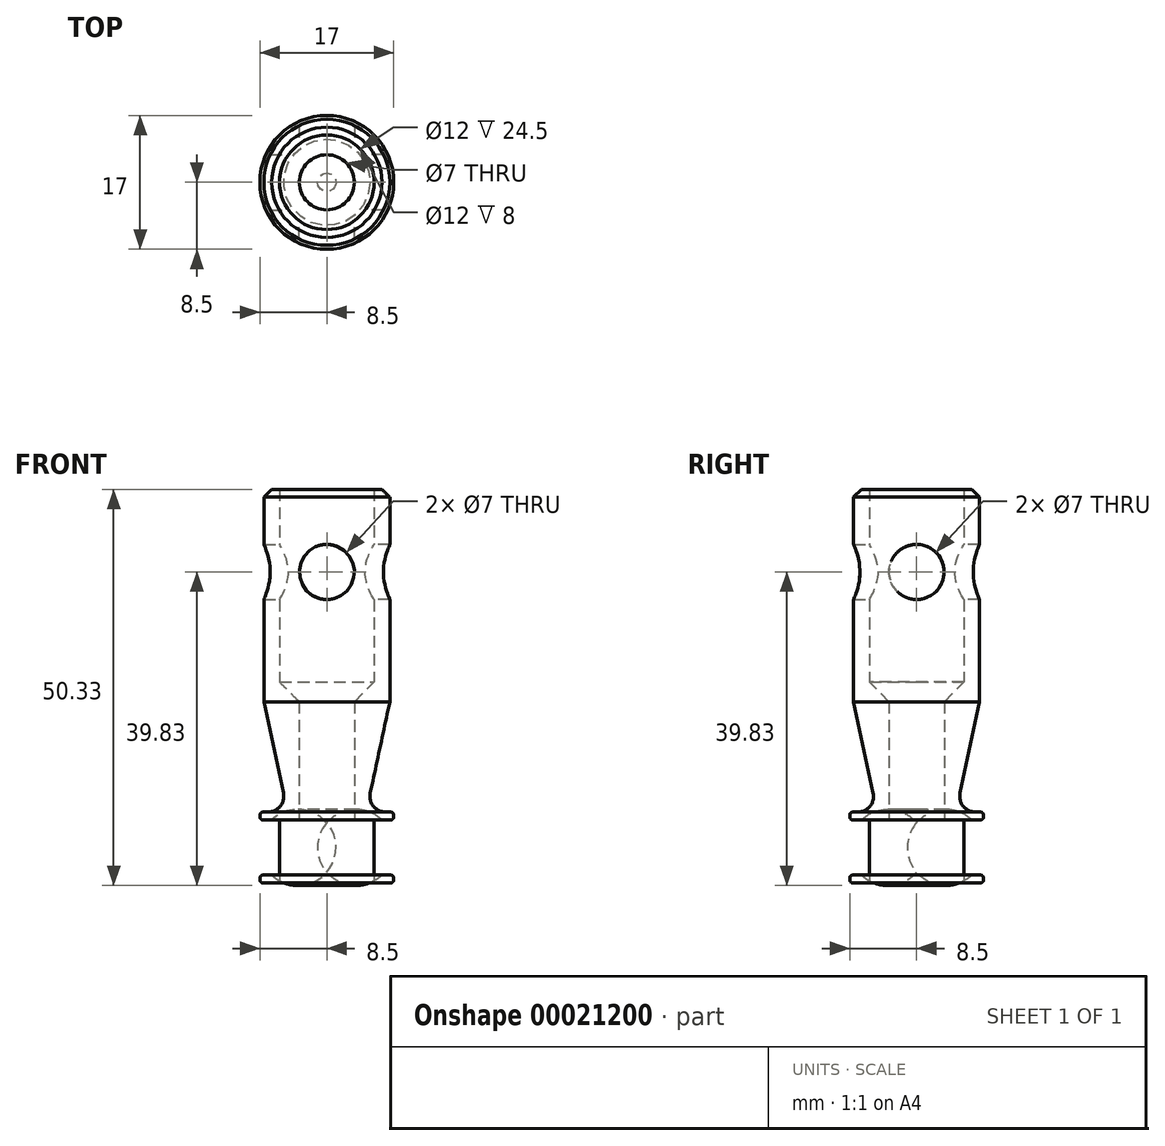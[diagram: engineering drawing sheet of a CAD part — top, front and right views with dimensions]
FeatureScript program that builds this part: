
annotation { "Feature Type Name" : "Feature", "Feature Type Description" : "" }
export const myFeature = defineFeature(function(context is Context, id is Id, definition is map)
    precondition{}
    {
        {
            var Q0;
            Q0=qCreatedBy(makeId("Front.planeOp"),FACE);
            var sketch = newSketch(context, id + "F0", { "sketchPlane" : qUnion([Q0])});
            skLineSegment(sketch, "E0", {"start": v(6, 0) * mm, "end": v(8.5, 0) * mm});
            skLineSegment(sketch, "E1", {"start": v(8.5, 0) * mm, "end": v(8.5, 1) * mm});
            skLineSegment(sketch, "E2", {"start": v(8.5, 1) * mm, "end": v(7, 1) * mm});
            skArc(sketch, "E3", {"start": v(7, 1) * mm, "mid": v(8.5, 4.5) * mm, "end": v(7, 8) * mm});
            skLineSegment(sketch, "E4", {"start": v(7, 8) * mm, "end": v(8.5, 8) * mm});
            skLineSegment(sketch, "E5", {"start": v(8.5, 8) * mm, "end": v(8.5, 9) * mm});
            skLineSegment(sketch, "E6", {"start": v(8.5, 9) * mm, "end": v(5, 9) * mm});
            skLineSegment(sketch, "E7", {"start": v(5, 9) * mm, "end": v(8, 23) * mm});
            skLineSegment(sketch, "E8", {"start": v(8, 23) * mm, "end": v(8, 50) * mm});
            skLineSegment(sketch, "E9", {"start": v(8, 50) * mm, "end": v(6, 50) * mm});
            skLineSegment(sketch, "E10", {"start": v(6, 50) * mm, "end": v(6, 25.5) * mm});
            skLineSegment(sketch, "E11", {"start": v(6, 25.5) * mm, "end": v(3.5, 23) * mm});
            skLineSegment(sketch, "E12", {"start": v(3.5, 23) * mm, "end": v(3.5, 8) * mm});
            skLineSegment(sketch, "E13", {"start": v(3.5, 8) * mm, "end": v(6, 8) * mm});
            skLineSegment(sketch, "E14", {"start": v(6, 8) * mm, "end": v(6, 0) * mm});
            skLineSegment(sketch, "E15", {"start": v(0, 0) * mm, "end": v(0, 60.76) * mm, "construction": true});
            skPoint(sketch, "E16", {"position": v(8.5, 4.5) * mm});
            skSolve(sketch);
        }
        {
            var Q0;
            Q0=qSketchRegion(id+"F0",true);
            var Q1;
            Q1=sQuery(id+"F0.wireOp",EDGE,"E15");
            revolve(context, id + "F1", {"entities" : qUnion([Q0]), "axis" : qUnion([Q1]), "revolveType" : RevolveType.FULL});
        }
        {
            var Q0;
            Q0=makeQuery(id+"F1.opRevolve","SWEPT_EDGE",EDGE,{"disambiguationData":[OSD([sQuery(id+"F0.wireOp",EDGE,"E6"),sQuery(id+"F0.wireOp",EDGE,"E7")])]});
            fillet(context, id + "F2", {"entities" : qUnion([Q0]), "radius" : 2 * mm, "tangentPropagation" : true, "allowEdgeOverflow" : false});
        }
        {
            var Q0;
            Q0=makeQuery(id+"F1.opRevolve","SWEPT_EDGE",EDGE,{"disambiguationData":[OSD([sQuery(id+"F0.wireOp",EDGE,"E0"),sQuery(id+"F0.wireOp",EDGE,"E1")])]});
            var Q1;
            Q1=makeQuery(id+"F1.opRevolve","SWEPT_EDGE",EDGE,{"disambiguationData":[OSD([sQuery(id+"F0.wireOp",EDGE,"E1"),sQuery(id+"F0.wireOp",EDGE,"E2")])]});
            var Q2;
            Q2=makeQuery(id+"F1.opRevolve","SWEPT_EDGE",EDGE,{"disambiguationData":[OSD([sQuery(id+"F0.wireOp",EDGE,"E4"),sQuery(id+"F0.wireOp",EDGE,"E5")])]});
            var Q3;
            Q3=makeQuery(id+"F1.opRevolve","SWEPT_EDGE",EDGE,{"disambiguationData":[OSD([sQuery(id+"F0.wireOp",EDGE,"E5"),sQuery(id+"F0.wireOp",EDGE,"E6")])]});
            fillet(context, id + "F3", {"entities" : qUnion([Q0, Q1, Q2, Q3]), "radius" : 0.4 * mm, "tangentPropagation" : true, "allowEdgeOverflow" : false});
        }
        {
            var Q0;
            Q0=qCreatedBy(makeId("Front.planeOp"),FACE);
            var sketch = newSketch(context, id + "F4", { "sketchPlane" : qUnion([Q0])});
            skCircle(sketch, "E17", {"center": v(0, 39.5) * mm, "radius": 3.5 * mm});
            skSolve(sketch);
        }
        {
            var Q0;
            Q0=qSketchRegion(id+"F4",true);
            extrude(context, id + "F5", {"entities" : qUnion([Q0]), "operationType" : NewBodyOperationType.REMOVE, "endBound" : BoundingType.THROUGH_ALL, "oppositeDirection" : true, "depth" : 25 * mm});
        }
        {
            var Q0;
            Q0=makeQuery(id+"F5.boolean.opBoolean","COPY",FACE,{"derivedFrom":makeQuery(id+"F5.opExtrude","SWEPT_FACE",FACE,{"disambiguationData":[OSD([sQuery(id+"F4.wireOp",EDGE,"E17")])]})});
            var Q1;
            Q1=makeQuery(id+"F1.opRevolve","SWEPT_FACE",FACE,{"disambiguationData":[OSD([sQuery(id+"F0.wireOp",EDGE,"E10")])]});
            circularPattern(context, id + "F6", {"faces" : qUnion([Q0]), "axis" : qUnion([Q1]), "angle" : 360 * degree, "instanceCount" : round(4), "equalSpace" : true, "patternType" : PatternType.FACE});
        }
        {
            var Q0;
            Q0=makeQuery(id+"F1.opRevolve","SWEPT_EDGE",EDGE,{"disambiguationData":[OSD([sQuery(id+"F0.wireOp",EDGE,"E8"),sQuery(id+"F0.wireOp",EDGE,"E9")])]});
            chamfer(context, id + "F7", {"entities" : qUnion([Q0]), "width" : 1 * mm, "tangentPropagation" : true});
        }
    });
